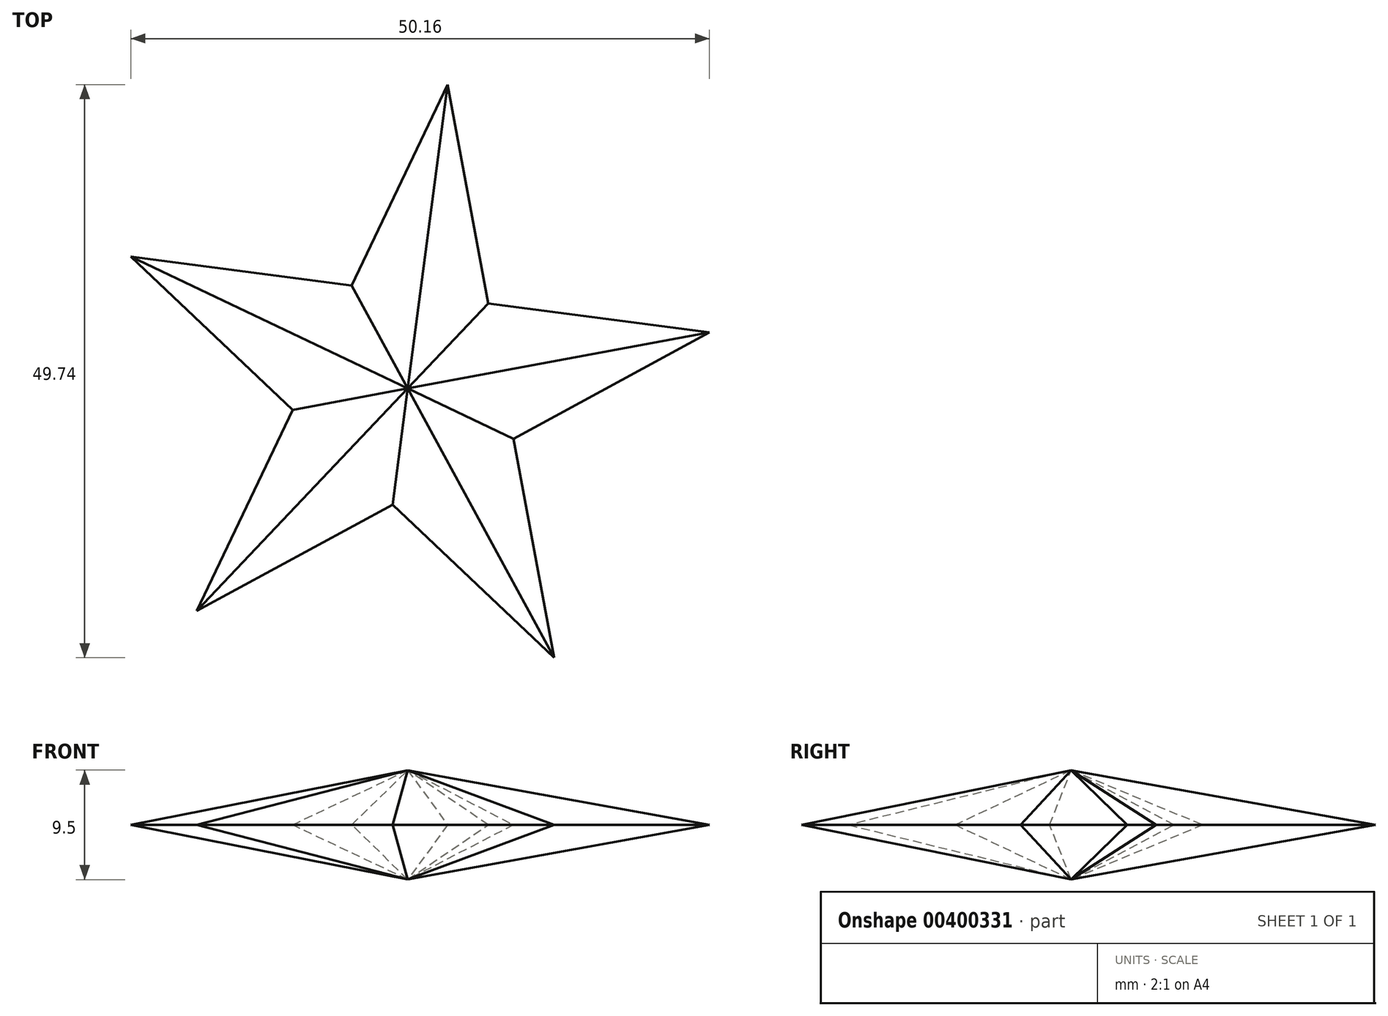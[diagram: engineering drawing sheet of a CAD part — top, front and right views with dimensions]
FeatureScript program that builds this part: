
annotation { "Feature Type Name" : "Feature", "Feature Type Description" : "" }
export const myFeature = defineFeature(function(context is Context, id is Id, definition is map)
    precondition{}
    {
        {
            var Q0;
            Q0=qCreatedBy(makeId("Top.planeOp"),FACE);
            var sketch = newSketch(context, id + "F0", { "sketchPlane" : qUnion([Q0])});
            skPoint(sketch, "E0.0.midPoint", {"position": v(-10.28, 18.9) * mm});
            skLineSegment(sketch, "E1", {"start": v(3.46, 26.37) * mm, "end": v(-4.85, 8.93) * mm});
            skLineSegment(sketch, "E2", {"start": v(12.7, -23.37) * mm, "end": v(9.17, -4.37) * mm});
            skLineSegment(sketch, "E3", {"start": v(-24.01, 11.44) * mm, "end": v(-4.85, 8.93) * mm});
            skLineSegment(sketch, "E4", {"start": v(-18.3, -19.3) * mm, "end": v(-1.32, -10.07) * mm});
            skLineSegment(sketch, "E5", {"start": v(12.7, -23.37) * mm, "end": v(-1.32, -10.07) * mm});
            skLineSegment(sketch, "E6.trimOffspring", {"start": v(7, 7.37) * mm, "end": v(26.15, 4.86) * mm});
            skLineSegment(sketch, "E7.trimOffspring", {"start": v(-9.99, -1.86) * mm, "end": v(-18.3, -19.3) * mm});
            skLineSegment(sketch, "E8.trimOffspring", {"start": v(-9.99, -1.86) * mm, "end": v(-24.01, 11.44) * mm});
            skLineSegment(sketch, "E9.trimOffspring", {"start": v(9.17, -4.37) * mm, "end": v(26.15, 4.86) * mm});
            skLineSegment(sketch, "E10.trimOffspring", {"start": v(7, 7.37) * mm, "end": v(3.46, 26.37) * mm});
            skLineSegment(sketch, "E11", {"start": v(3.46, 26.37) * mm, "end": v(0, 0) * mm});
            skLineSegment(sketch, "E12", {"start": v(-9.99, -1.86) * mm, "end": v(0, 0) * mm});
            skLineSegment(sketch, "E13", {"start": v(-4.85, 8.93) * mm, "end": v(0, 0) * mm});
            skLineSegment(sketch, "E14", {"start": v(7, 7.37) * mm, "end": v(0, 0) * mm});
            skLineSegment(sketch, "E15", {"start": v(9.17, -4.37) * mm, "end": v(0, 0) * mm});
            skLineSegment(sketch, "E16", {"start": v(0, 0) * mm, "end": v(-24.01, 11.44) * mm});
            skLineSegment(sketch, "E17", {"start": v(-18.3, -19.3) * mm, "end": v(0, 0) * mm});
            skLineSegment(sketch, "E18", {"start": v(12.7, -23.37) * mm, "end": v(0, 0) * mm});
            skLineSegment(sketch, "E19", {"start": v(-1.32, -10.07) * mm, "end": v(0, 0) * mm});
            skLineSegment(sketch, "E20", {"start": v(26.15, 4.86) * mm, "end": v(0, 0) * mm});
            skSolve(sketch);
        }
        {
            var Q0;
            Q0 = qSketchRegion(id + "F0", true);
            extrude(context, id + "F1", {"entities" : qUnion([Q0]), "depth" : 25.4 * mm, "hasDraft" : true, "draftAngle" : 60 * degree, "draftPullDirection" : true, "hasSecondDirection" : true, "secondDirectionOppositeDirection" : true, "secondDirectionDepth" : 25.4 * mm, "hasSecondDirectionDraft" : true, "secondDirectionDraftAngle" : 60 * degree, "secondDirectionDraftPullDirection" : true});
        }
    });
